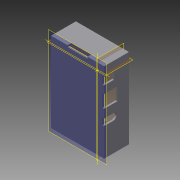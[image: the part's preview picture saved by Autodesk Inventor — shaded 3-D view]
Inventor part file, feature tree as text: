
AUTODESK INVENTOR PART (.ipt)
format: ipt  version: 2015 (Build 190159000, 159)  size: 206,336 bytes
history: native  units: mm
features: sketch x11, projected_geometry x8, extrude x6, sweep x1
ambient origin geometry x8: Origin, YZ Plane, XZ Plane, XY Plane, X Axis, Y Axis, Z Axis, Center Point
bodies: Solid1 (feature_tree)
feature tree (26):
  sketch  "Sketch1"  dims[d0=2.5mm d1=20.0mm d3=49.0mm d4=20.0mm d6=58.0mm]
  extrude  "Extrusion1"  Depth=20.0mm
  extrude  "Extrusion2"  Depth=10.0mm
  sketch  "Sketch4"  dims[d14=3.5mm d15=2.0mm]
  sketch  "Sketch5"  dims[d16=2.0mm d17=0.0mm d18=2.0mm]
  sketch  "3D Sketch1"
  sweep  "Sweep2"
  extrude  "Extrusion3"  Depth=2.0mm
  extrude  "Extrusion4"  Depth=2.0mm
  extrude  "Extrusion5"  TaperAngle=0.0deg  [1 undecoded]
  extrude  "Extrusion6"  Depth=2.0mm TaperAngle=0.0deg
  sketch  "Sketch2"  dims[d9=10.0mm d10=0.0mm d11=3.5mm]
  sketch  "Sketch3"  dims[d12=27.0mm d13=3.5mm]
  projected_geometry  "Projected Loop1"
  projected_geometry  "Projected Loop2"
  projected_geometry  "Projected Loop3"
  projected_geometry  "Projected Loop4"
  sketch  "3D Sketch2"
  sketch  "Sketch6"  dims[d19=30.0mm d23=0.0mm d24=0.0mm]
  sketch  "Sketch7"  dims[d25=5.0mm d26=2.0mm d27=0.0mm]
  sketch  "Sketch8"  dims[d28=11.0mm]
  sketch  "Sketch9"  dims[d29=12.0mm d30=9.0mm d31=9.0mm d32=15.5mm d33=16.0mm d34=10.0mm d35=8.0mm d36=15.0mm d37=2.0mm d38=0.0mm d39=20.0mm d40=20.0mm d41=5.0mm d42=2.0mm d43=0.0mm d44=5.0mm d45=5.0mm d46=5.0mm d47=5.0mm d48=4.0mm d49=0.0mm]
  projected_geometry  "Projected Loop5"
  projected_geometry  "Projected Loop6"
  projected_geometry  "Projected Loop7"
  projected_geometry  "Projected Loop8"
note: 1 required parameter value undecoded (feature->parameter linkage not recoverable at this tier; creation-order binding heuristic only, values carry confidence <= 0.55)
